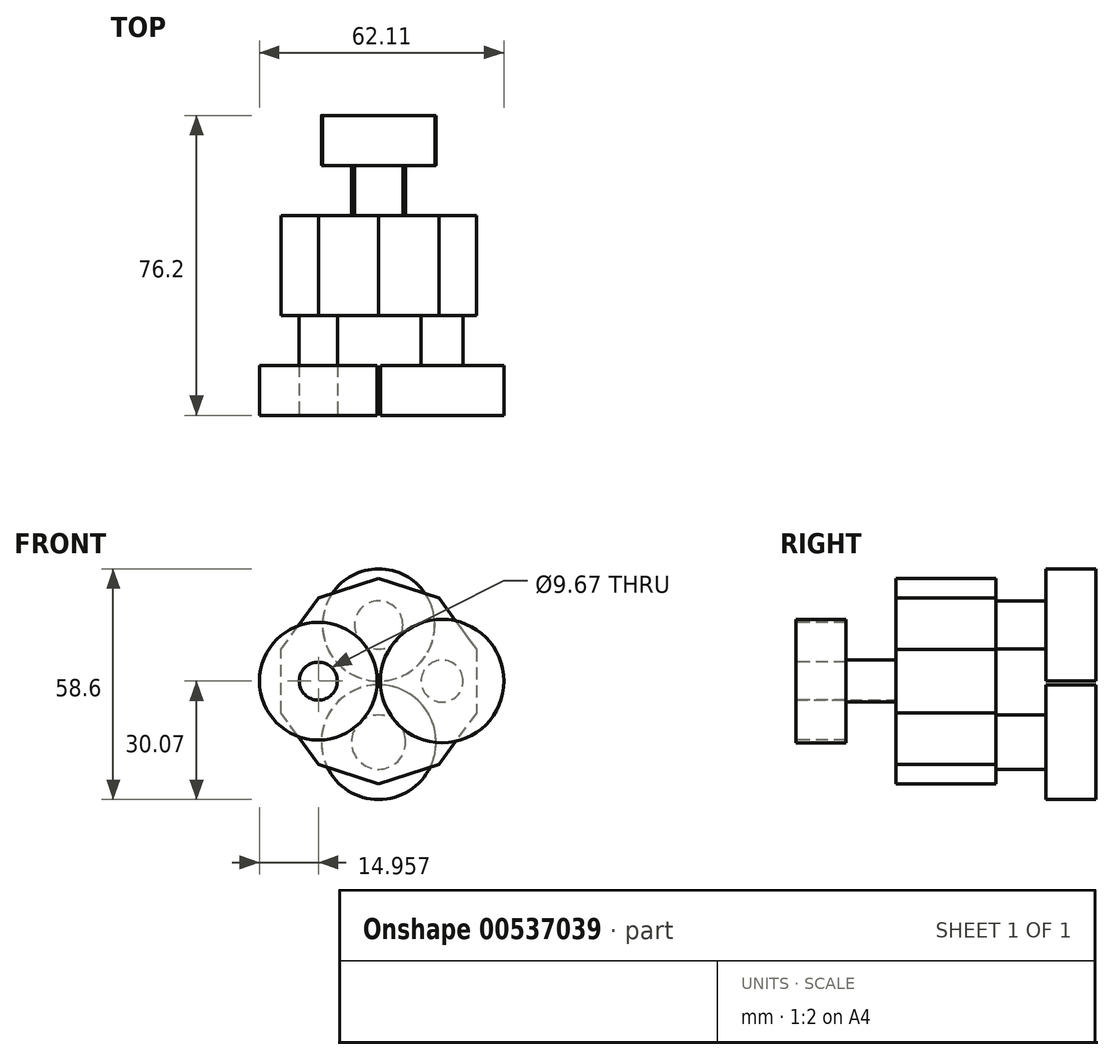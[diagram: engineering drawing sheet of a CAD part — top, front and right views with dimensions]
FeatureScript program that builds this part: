
annotation { "Feature Type Name" : "Feature", "Feature Type Description" : "" }
export const myFeature = defineFeature(function(context is Context, id is Id, definition is map)
    precondition{}
    {
        {
            var Q0;
            Q0=qCreatedBy(makeId("Front.planeOp"),FACE);
            var sketch = newSketch(context, id + "F0", { "sketchPlane" : qUnion([Q0])});
            skCircle(sketch, "E0.cCircle", {"center": v(0, 0) * mm, "radius": 24.8 * mm, "construction": true});
            skLineSegment(sketch, "E0.0", {"start": v(-24.8, -8.06) * mm, "end": v(-24.8, 8.06) * mm});
            skLineSegment(sketch, "E0.1", {"start": v(-24.8, 8.06) * mm, "end": v(-15.33, 21.1) * mm});
            skLineSegment(sketch, "E0.2", {"start": v(-15.33, 21.1) * mm, "end": v(0, 26.09) * mm});
            skLineSegment(sketch, "E0.3", {"start": v(0, 26.09) * mm, "end": v(15.33, 21.1) * mm});
            skLineSegment(sketch, "E0.4", {"start": v(15.33, 21.1) * mm, "end": v(24.8, 8.06) * mm});
            skLineSegment(sketch, "E0.5", {"start": v(24.8, 8.06) * mm, "end": v(24.8, -8.06) * mm});
            skLineSegment(sketch, "E0.6", {"start": v(24.8, -8.06) * mm, "end": v(15.33, -21.1) * mm});
            skLineSegment(sketch, "E0.7", {"start": v(15.33, -21.1) * mm, "end": v(0, -26.09) * mm});
            skLineSegment(sketch, "E0.8", {"start": v(0, -26.09) * mm, "end": v(-15.33, -21.1) * mm});
            skLineSegment(sketch, "E0.9", {"start": v(-15.33, -21.1) * mm, "end": v(-24.8, -8.06) * mm});
            skPoint(sketch, "E0.0.midPoint", {"position": v(-24.8, 0) * mm});
            skSolve(sketch);
        }
        {
            var Q0;
            Q0 = qSketchRegion(id + "F0", true);
            extrude(context, id + "F1", {"entities" : qUnion([Q0]), "depth" : 25.4 * mm, "offsetDistance" : 25.4 * mm});
        }
        {
            var Q0;
            Q0=makeQuery(id+"F1.opExtrude","CAP_FACE",FACE,{"disambiguationData":[OSD([sQuery(id+"F0.wireOp",EDGE,"E0.0"),sQuery(id+"F0.wireOp",EDGE,"E0.1"),sQuery(id+"F0.wireOp",EDGE,"E0.2"),sQuery(id+"F0.wireOp",EDGE,"E0.3"),sQuery(id+"F0.wireOp",EDGE,"E0.4"),sQuery(id+"F0.wireOp",EDGE,"E0.5"),sQuery(id+"F0.wireOp",EDGE,"E0.6"),sQuery(id+"F0.wireOp",EDGE,"E0.7"),sQuery(id+"F0.wireOp",EDGE,"E0.8"),sQuery(id+"F0.wireOp",EDGE,"E0.9")])],"isStart":false});
            var sketch = newSketch(context, id + "F2", { "sketchPlane" : qUnion([Q0])});
            skCircle(sketch, "E1", {"center": v(0, 14.58) * mm, "radius": 4.44 * mm});
            skPoint(sketch, "E1.centerSnap0", {"position": v(-20.07, 14.58) * mm});
            skCircle(sketch, "E2", {"center": v(0, -13.02) * mm, "radius": 4.74 * mm});
            skCircle(sketch, "E3", {"center": v(-15.33, 0) * mm, "radius": 4.83 * mm});
            skCircle(sketch, "E4", {"center": v(16.13, 0) * mm, "radius": 5.34 * mm});
            skSolve(sketch);
        }
        {
            var Q0;
            Q0=makeQuery(id+"F2.imprint","IMPRINT",FACE,{"disambiguationData":[TD([[makeQuery(id+"F2.imprint","IMPRINT",EDGE,{"derivedFrom":sQuery(id+"F2.wireOp",EDGE,"E3")}),1.0]])]});
            var Q1;
            Q1=makeQuery(id+"F2.imprint","IMPRINT",FACE,{"disambiguationData":[TD([[makeQuery(id+"F2.imprint","IMPRINT",EDGE,{"derivedFrom":sQuery(id+"F2.wireOp",EDGE,"E4")}),1.0]])]});
            extrude(context, id + "F3", {"entities" : qUnion([Q0, Q1]), "operationType" : NewBodyOperationType.ADD, "depth" : 25.4 * mm, "offsetDistance" : 25.4 * mm});
        }
        {
            var Q0;
            Q0=makeQuery(id+"F1.opExtrude","CAP_FACE",FACE,{"disambiguationData":[OSD([sQuery(id+"F0.wireOp",EDGE,"E0.0"),sQuery(id+"F0.wireOp",EDGE,"E0.1"),sQuery(id+"F0.wireOp",EDGE,"E0.2"),sQuery(id+"F0.wireOp",EDGE,"E0.3"),sQuery(id+"F0.wireOp",EDGE,"E0.4"),sQuery(id+"F0.wireOp",EDGE,"E0.5"),sQuery(id+"F0.wireOp",EDGE,"E0.6"),sQuery(id+"F0.wireOp",EDGE,"E0.7"),sQuery(id+"F0.wireOp",EDGE,"E0.8"),sQuery(id+"F0.wireOp",EDGE,"E0.9")])],"isStart":false});
            var sketch = newSketch(context, id + "F4", { "sketchPlane" : qUnion([Q0])});
            skCircle(sketch, "E5", {"center": v(0, 14.27) * mm, "radius": 6.14 * mm});
            skCircle(sketch, "E6", {"center": v(0, -15.5) * mm, "radius": 6.89 * mm});
            skSolve(sketch);
        }
        {
            var Q0;
            Q0=makeQuery(id+"F4.imprint","IMPRINT",FACE,{"disambiguationData":[TD([[makeQuery(id+"F4.imprint","IMPRINT",EDGE,{"derivedFrom":sQuery(id+"F4.wireOp",EDGE,"E5")}),1.0]])]});
            var Q1;
            Q1=makeQuery(id+"F4.imprint","IMPRINT",FACE,{"disambiguationData":[TD([[makeQuery(id+"F4.imprint","IMPRINT",EDGE,{"derivedFrom":sQuery(id+"F4.wireOp",EDGE,"E6")}),1.0]])]});
            extrude(context, id + "F5", {"entities" : qUnion([Q0, Q1]), "operationType" : NewBodyOperationType.ADD, "oppositeDirection" : true, "depth" : 50.8 * mm, "offsetDistance" : 25.4 * mm});
        }
        {
            var Q0;
            Q0=makeQuery(id+"F3.opExtrude","CAP_FACE",FACE,{"disambiguationData":[OSD([sQuery(id+"F2.wireOp",EDGE,"E3")])],"isStart":false});
            var sketch = newSketch(context, id + "F6", { "sketchPlane" : qUnion([Q0])});
            skCircle(sketch, "E7", {"center": v(-15.33, 0) * mm, "radius": 14.96 * mm});
            skSolve(sketch);
        }
        {
            var Q0;
            Q0=makeQuery(id+"F6.imprint","IMPRINT",FACE,{"disambiguationData":[TD([[makeQuery(id+"F6.imprint","IMPRINT",EDGE,{"derivedFrom":sQuery(id+"F6.wireOp",EDGE,"E7")}),1.0]])]});
            extrude(context, id + "F7", {"entities" : qUnion([Q0]), "oppositeDirection" : true, "depth" : 12.7 * mm, "offsetDistance" : 25.4 * mm});
        }
        {
            var Q0;
            Q0=makeQuery(id+"F3.opExtrude","CAP_FACE",FACE,{"disambiguationData":[OSD([sQuery(id+"F2.wireOp",EDGE,"E4")])],"isStart":false});
            var sketch = newSketch(context, id + "F8", { "sketchPlane" : qUnion([Q0])});
            skCircle(sketch, "E8", {"center": v(16.13, 0) * mm, "radius": 15.7 * mm});
            skSolve(sketch);
        }
        {
            var Q0;
            Q0=makeQuery(id+"F8.imprint","IMPRINT",FACE,{"disambiguationData":[TD([[makeQuery(id+"F8.imprint","IMPRINT",EDGE,{"derivedFrom":sQuery(id+"F8.wireOp",EDGE,"E8")}),1.0]])]});
            extrude(context, id + "F9", {"entities" : qUnion([Q0]), "operationType" : NewBodyOperationType.ADD, "oppositeDirection" : true, "depth" : 12.7 * mm, "offsetDistance" : 25.4 * mm});
        }
        {
            var Q0;
            Q0=makeQuery(id+"F5.opExtrude","CAP_FACE",FACE,{"disambiguationData":[OSD([sQuery(id+"F4.wireOp",EDGE,"E5")])],"isStart":false});
            var sketch = newSketch(context, id + "F10", { "sketchPlane" : qUnion([Q0])});
            skCircle(sketch, "E9", {"center": v(0, 14.27) * mm, "radius": 14.27 * mm});
            skSolve(sketch);
        }
        {
            var Q0;
            Q0=makeQuery(id+"F10.imprint","IMPRINT",FACE,{"disambiguationData":[TD([[makeQuery(id+"F10.imprint","IMPRINT",EDGE,{"derivedFrom":sQuery(id+"F10.wireOp",EDGE,"E9")}),1.0]])]});
            extrude(context, id + "F11", {"entities" : qUnion([Q0]), "operationType" : NewBodyOperationType.ADD, "oppositeDirection" : true, "depth" : 12.7 * mm, "offsetDistance" : 25.4 * mm});
        }
        {
            var Q0;
            Q0=makeQuery(id+"F5.opExtrude","CAP_FACE",FACE,{"disambiguationData":[OSD([sQuery(id+"F4.wireOp",EDGE,"E6")])],"isStart":false});
            var sketch = newSketch(context, id + "F12", { "sketchPlane" : qUnion([Q0])});
            skCircle(sketch, "E10", {"center": v(0, -15.5) * mm, "radius": 14.56 * mm});
            skSolve(sketch);
        }
        {
            var Q0;
            Q0=makeQuery(id+"F12.imprint","IMPRINT",FACE,{"disambiguationData":[TD([[makeQuery(id+"F12.imprint","IMPRINT",EDGE,{"derivedFrom":sQuery(id+"F12.wireOp",EDGE,"E10")}),1.0]])]});
            extrude(context, id + "F13", {"entities" : qUnion([Q0]), "operationType" : NewBodyOperationType.ADD, "oppositeDirection" : true, "depth" : 12.7 * mm, "offsetDistance" : 25.4 * mm});
        }
    });
